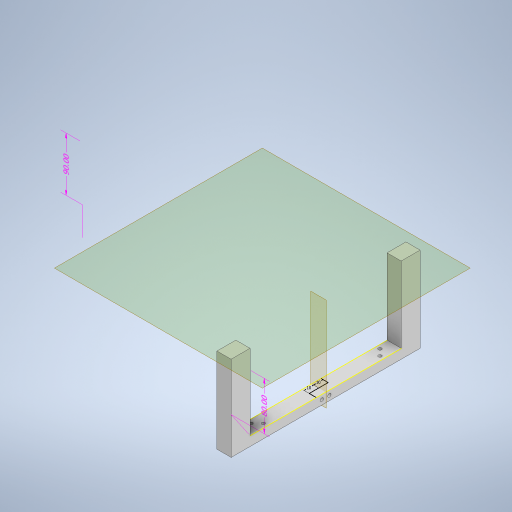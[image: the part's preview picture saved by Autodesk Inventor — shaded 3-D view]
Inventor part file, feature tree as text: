
AUTODESK INVENTOR PART (.ipt)
format: ipt  version: 2023 (Build 270158000, 158)  size: 375,808 bytes
history: native  units: mm
features: sketch x9, extrude x5, other x4, hole x3, plane x2, split x1
ambient origin geometry x8: Origin, YZ Plane, XZ Plane, XY Plane, X Axis, Y Axis, Z Axis, Center Point
bodies: Body1 (feature_tree), Body2 (feature_tree)
feature tree (24):
  other  "Sólido1"
  other  "Anotaciones"
  extrude  "Extrusión1"  Depth=200.0mm
  hole  "Agujero1"  [1 undecoded]
  extrude  "Extrusión2"  Depth=15.0mm
  extrude  "Extrusión3"  Depth=80.0mm TaperAngle=0.0deg
  extrude  "Extrusión4"  Depth=200.0mm
  extrude  "Extrusión5"  Depth=20.0mm
  hole  "Agujero2"  [1 undecoded]
  plane  "Plano de trabajo1"
  split  "Dividir1"
  sketch  "Boceto9"  dims[d37=20.0mm d38=20.0mm]
  plane  "Plano de trabajo2"
  hole  "Agujero3"  [1 undecoded]
  sketch  "Boceto2"  dims[d7=15.0mm d8=200.0mm]
  sketch  "Boceto3"  dims[d9=10.0mm d10=0.0mm]
  sketch  "Boceto4"  dims[d12=1.75mm d13=1.75mm d14=1.75mm d15=1.75mm d16=10.0mm d17=10.0mm d19=30.0mm]
  sketch  "Boceto5"  dims[d20=3.5mm d21=6.0mm d22=4.0mm d23=2.0mm d24=90.0deg d25=8.0mm d26=20.594885mm d27=15.0mm]
  sketch  "Boceto6"  dims[d28=20.0mm d29=80.0mm d30=0.0mm]
  sketch  "Boceto7"  dims[d31=48.0mm d32=200.0mm]
  sketch  "Boceto8"  dims[d33=110.0mm d34=0.0mm d36=20.0mm]
  sketch  "Boceto10"  dims[d39=90.0mm d40=0.0mm d42=10.0mm d43=30.0mm d44=0.0mm d46=1.75mm d47=1.75mm d48=1.75mm d49=1.75mm d50=10.0mm d51=10.0mm d52=15.0mm d56=3.5mm d57=6.0mm d58=4.0mm d59=2.0mm d60=90.0deg d61=8.0mm d62=20.594885mm d63=10.0mm d65=10.0mm d66=10.0mm d67=31.75mm d70=15.0mm d74=200.0mm d78=20.0mm d82=90.0deg d83=10.0mm d84=10.0mm d85=3.5mm d86=4.0mm d87=5.0mm d88=3.5mm d89=6.0mm d90=4.0mm d91=2.0mm d92=90.0deg d93=8.0mm d94=20.594885mm d75=1.454734mm d76=6.982969mm d77=80.0mm d79=4.097996mm d80=1.406125mm d81=90.0mm]
  other  "Cota lineal 2"
  other  "Cota lineal 3"
note: 3 required parameter values undecoded (feature->parameter linkage not recoverable at this tier; creation-order binding heuristic only, values carry confidence <= 0.55)
